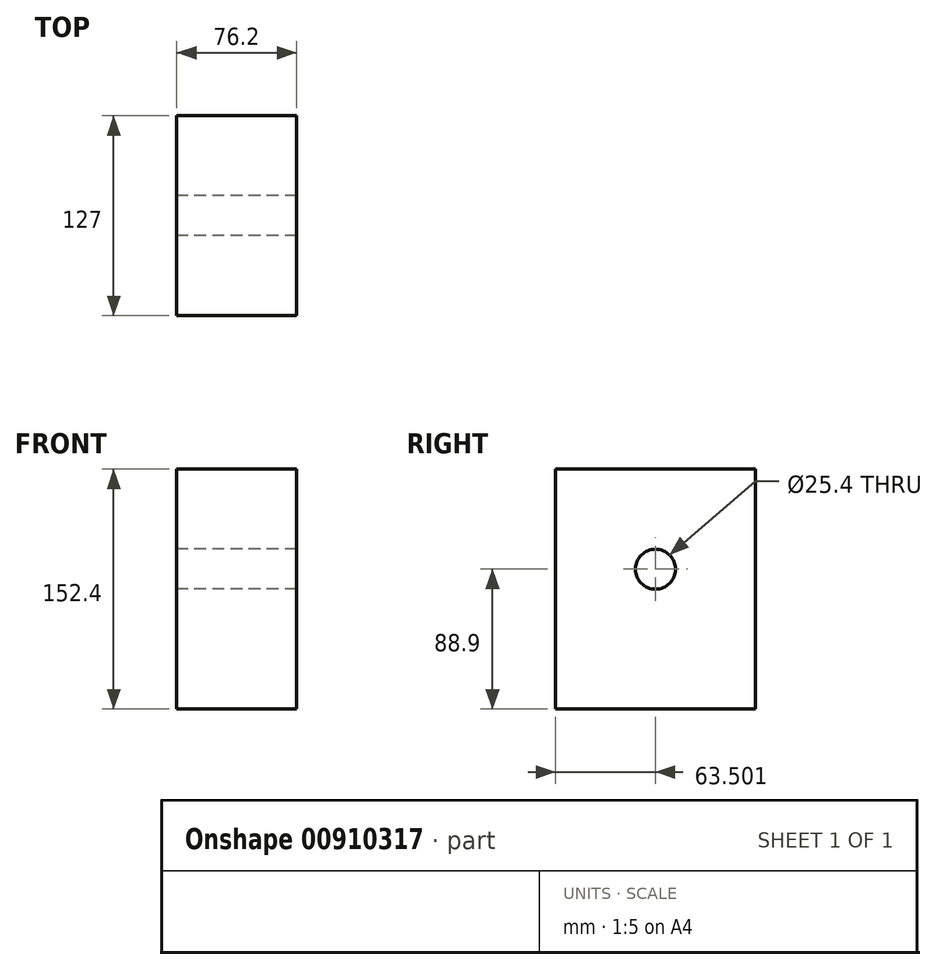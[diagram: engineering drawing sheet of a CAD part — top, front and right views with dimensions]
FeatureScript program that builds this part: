
annotation { "Feature Type Name" : "Feature", "Feature Type Description" : "" }
export const myFeature = defineFeature(function(context is Context, id is Id, definition is map)
    precondition{}
    {
        {
            var Q0;
            Q0=qCreatedBy(makeId("Top.planeOp"),FACE);
            var sketch = newSketch(context, id + "F0", { "sketchPlane" : qUnion([Q0])});
            skLineSegment(sketch, "E0.bottom", {"start": v(-128.72, 86.75) * mm, "end": v(-52.52, 86.75) * mm});
            skLineSegment(sketch, "E0.top", {"start": v(-128.72, -40.25) * mm, "end": v(-52.52, -40.25) * mm});
            skLineSegment(sketch, "E0.left", {"start": v(-128.72, 86.75) * mm, "end": v(-128.72, -40.25) * mm});
            skLineSegment(sketch, "E0.right", {"start": v(-52.52, 86.75) * mm, "end": v(-52.52, -40.25) * mm});
            skSolve(sketch);
        }
        {
            var Q0;
            Q0=makeQuery(id+"F0.imprint","IMPRINT",FACE,{"disambiguationData":[TD([[makeQuery(id+"F0.imprint","IMPRINT",EDGE,{"derivedFrom":sQuery(id+"F0.wireOp",EDGE,"E0.bottom")}),-1.0]])]});
            extrude(context, id + "F1", {"entities" : qUnion([Q0]), "depth" : 152.4 * mm, "offsetDistance" : 25.4 * mm});
        }
        {
            var Q0;
            Q0=makeQuery(id+"F1.opExtrude","SWEPT_FACE",FACE,{"disambiguationData":[OSD([sQuery(id+"F0.wireOp",EDGE,"E0.left")])]});
            var sketch = newSketch(context, id + "F2", { "sketchPlane" : qUnion([Q0])});
            skCircle(sketch, "E1", {"center": v(-23.25, 88.9) * mm, "radius": 12.7 * mm});
            skSolve(sketch);
        }
        {
            var Q0;
            Q0=makeQuery(id+"F2.imprint","IMPRINT",FACE,{"disambiguationData":[TD([[makeQuery(id+"F2.imprint","IMPRINT",EDGE,{"derivedFrom":sQuery(id+"F2.wireOp",EDGE,"E1")}),1.0]])]});
            extrude(context, id + "F3", {"entities" : qUnion([Q0]), "operationType" : NewBodyOperationType.REMOVE, "endBound" : BoundingType.THROUGH_ALL, "oppositeDirection" : true, "depth" : 25.4 * mm, "offsetDistance" : 25.4 * mm});
        }
    });
